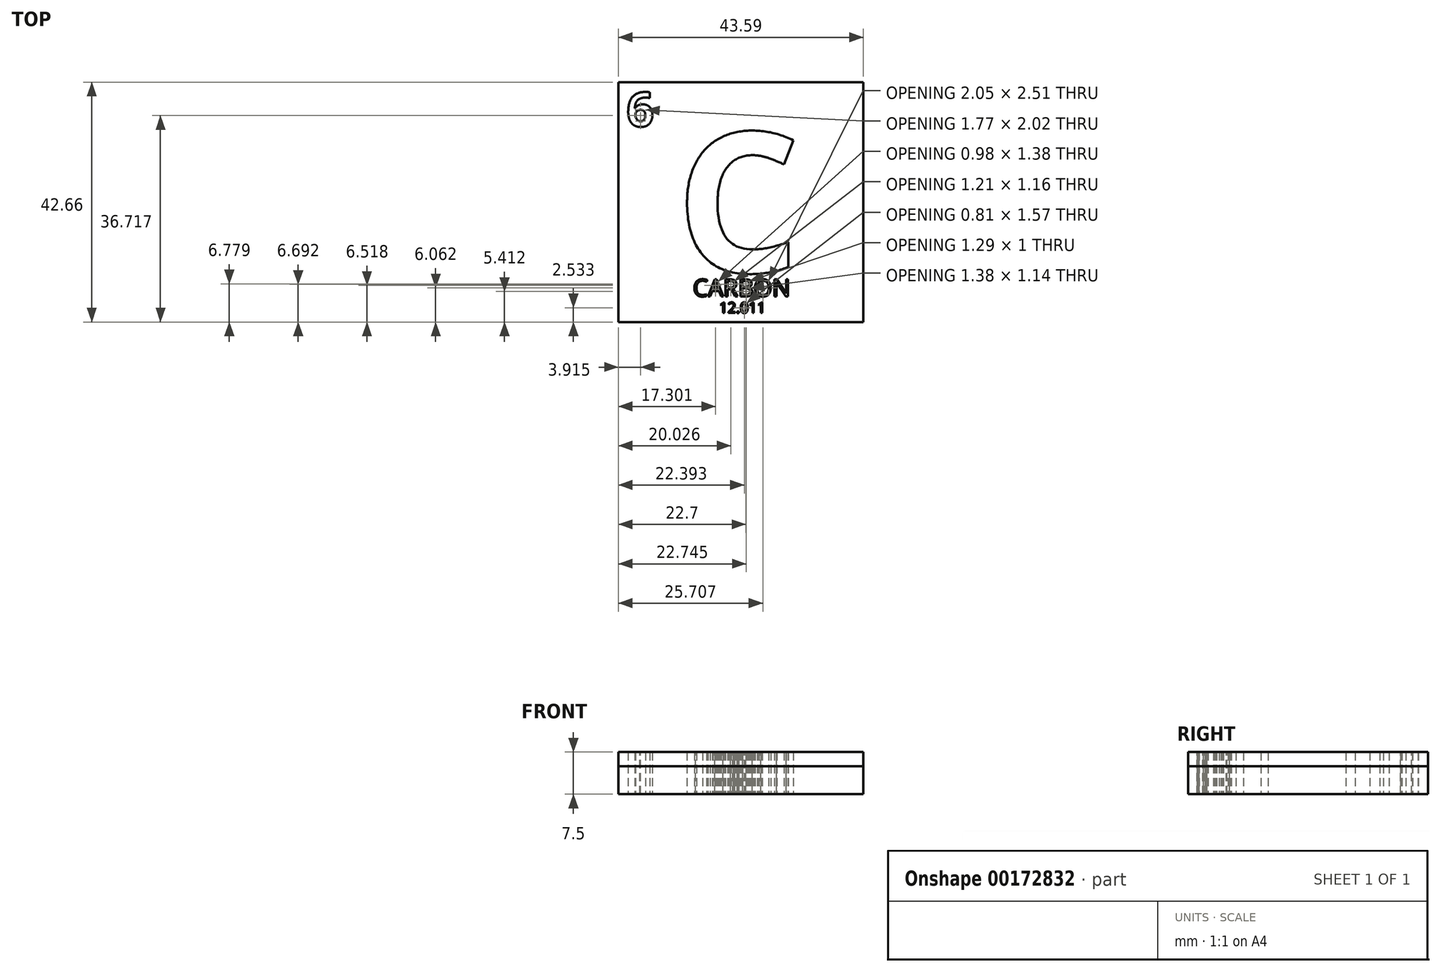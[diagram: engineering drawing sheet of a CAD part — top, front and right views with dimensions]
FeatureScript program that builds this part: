
annotation { "Feature Type Name" : "Feature", "Feature Type Description" : "" }
export const myFeature = defineFeature(function(context is Context, id is Id, definition is map)
    precondition{}
    {
        {
            var Q0;
            Q0=qCreatedBy(makeId("Top.planeOp"),FACE);
            var sketch = newSketch(context, id + "F0", { "sketchPlane" : qUnion([Q0])});
            skLineSegment(sketch, "E0.bottom", {"start": v(-21.8, 22.06) * mm, "end": v(21.79, 22.06) * mm});
            skLineSegment(sketch, "E0.top", {"start": v(-21.8, -20.6) * mm, "end": v(21.79, -20.6) * mm});
            skLineSegment(sketch, "E0.left", {"start": v(-21.8, 22.06) * mm, "end": v(-21.8, -20.6) * mm});
            skLineSegment(sketch, "E0.right", {"start": v(21.79, 22.06) * mm, "end": v(21.79, -20.6) * mm});
            skSolve(sketch);
        }
        {
            var Q0;
            Q0 = qSketchRegion(id + "F0", true);
            extrude(context, id + "F1", {"entities" : qUnion([Q0]), "depth" : 5 * mm});
        }
        {
            var Q0;
            Q0=qCreatedBy(makeId("Top.planeOp"),FACE);
            var sketch = newSketch(context, id + "F2", { "sketchPlane" : qUnion([Q0])});
            skText(sketch, "E1", { "text": "C", "fontName": "OpenSans-Bold.ttf"});
            skText(sketch, "E2", { "text": "6", "fontName": "OpenSans-Bold.ttf"});
            skText(sketch, "E3", { "text": "CARBON", "fontName": "OpenSans-Regular.ttf"});
            skText(sketch, "E4", { "text": "12.011", "fontName": "OpenSans-Regular.ttf"});
            const initialGuessF2  = {"E1": [-0.0116, -0.01175, 1, 0, 0.02506], "E2": [-0.02035, 0.01416, 1, 0, 0.00614], "E3": [-0.00854, -0.01606, 1, 0, 0.00307], "E4": [-0.00388, -0.01901, 1, 0, 0.0019]};
            skSetInitialGuess(sketch, initialGuessF2);
            skSolve(sketch);
        }
        {
            var Q0;
            Q0 = qSketchRegion(id + "F2", true);
            extrude(context, id + "F3", {"entities" : qUnion([Q0]), "depth" : 7.5 * mm});
        }
        {
            var Q0;
            Q0=makeQuery(id+"F0.imprint","IMPRINT",FACE,{"disambiguationData":[TD([[makeQuery(id+"F0.imprint","IMPRINT",EDGE,{"derivedFrom":sQuery(id+"F0.wireOp",EDGE,"E0.bottom")}),-1.0]])]});
            extrude(context, id + "F4", {"entities" : qUnion([Q0]), "depth" : 7.5 * mm});
        }
    });
